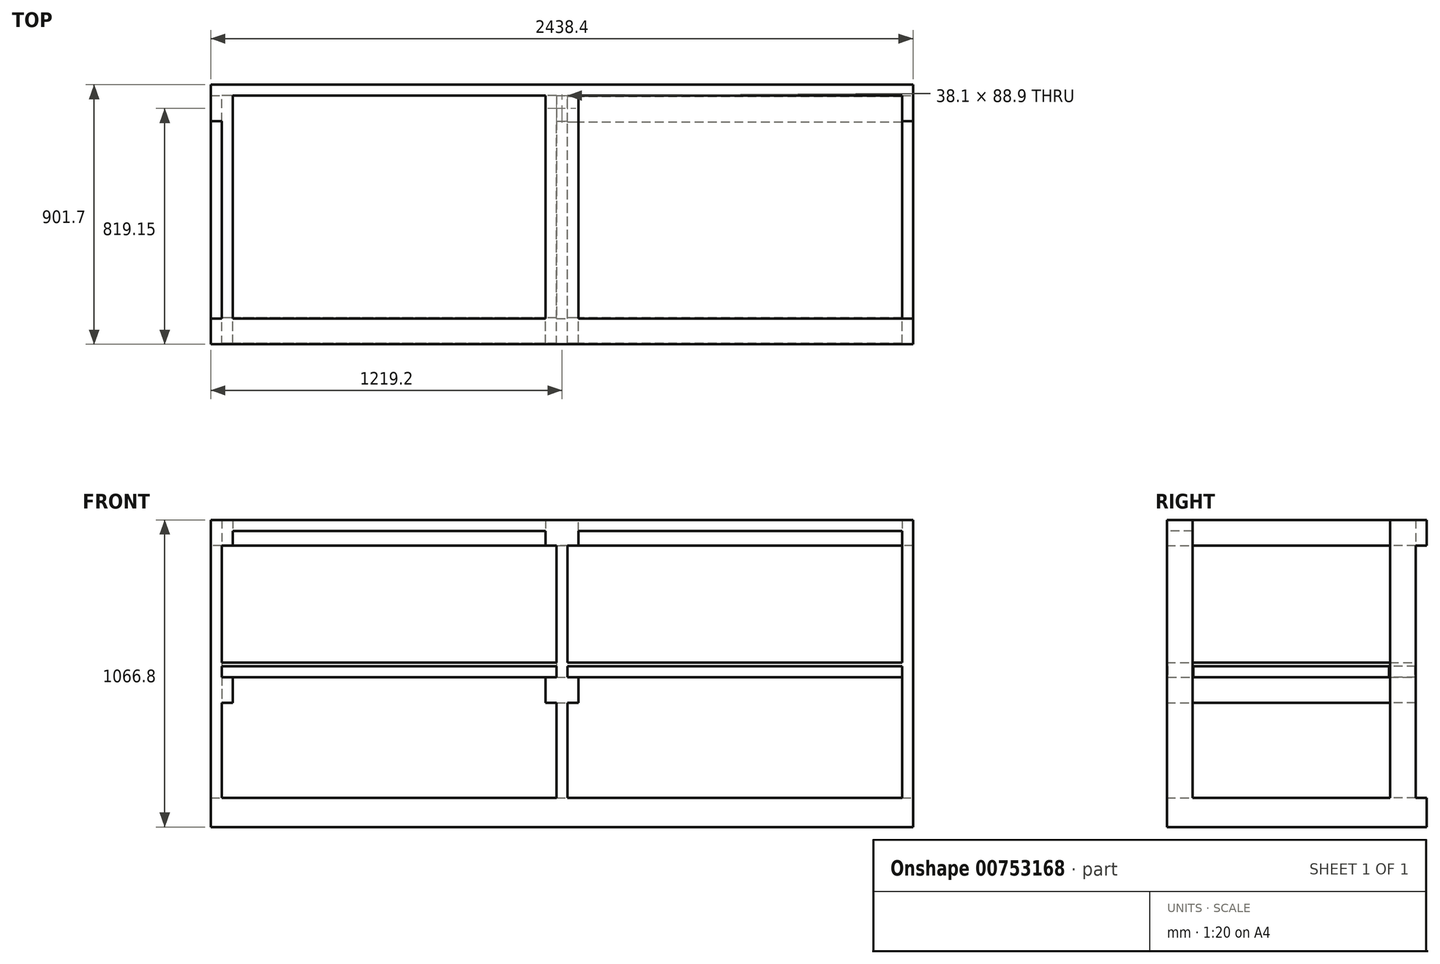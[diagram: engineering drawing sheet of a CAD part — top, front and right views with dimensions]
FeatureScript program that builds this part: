
annotation { "Feature Type Name" : "Feature", "Feature Type Description" : "" }
export const myFeature = defineFeature(function(context is Context, id is Id, definition is map)
    precondition{}
    {
        {
            var Q0;
            Q0=qCreatedBy(makeId("Top.planeOp"),FACE);
            var sketch = newSketch(context, id + "F0", { "sketchPlane" : qUnion([Q0])});
            skLineSegment(sketch, "E0.bottom", {"start": v(0, 0) * mm, "end": v(38.1, 0) * mm});
            skLineSegment(sketch, "E0.top", {"start": v(0, 88.9) * mm, "end": v(38.1, 88.9) * mm});
            skLineSegment(sketch, "E0.left", {"start": v(0, 0) * mm, "end": v(0, 88.9) * mm});
            skLineSegment(sketch, "E0.right", {"start": v(38.1, 0) * mm, "end": v(38.1, 88.9) * mm});
            skLineSegment(sketch, "E1.bottom", {"start": v(0, 774.7) * mm, "end": v(38.1, 774.7) * mm});
            skLineSegment(sketch, "E1.top", {"start": v(0, 863.6) * mm, "end": v(38.1, 863.6) * mm});
            skLineSegment(sketch, "E1.left", {"start": v(0, 774.7) * mm, "end": v(0, 863.6) * mm});
            skLineSegment(sketch, "E1.right", {"start": v(38.1, 774.7) * mm, "end": v(38.1, 863.6) * mm});
            skLineSegment(sketch, "E2.bottom", {"start": v(1200.15, 0) * mm, "end": v(1238.25, 0) * mm});
            skLineSegment(sketch, "E2.top", {"start": v(1200.15, 88.9) * mm, "end": v(1238.25, 88.9) * mm});
            skLineSegment(sketch, "E2.left", {"start": v(1200.15, 0) * mm, "end": v(1200.15, 88.9) * mm});
            skLineSegment(sketch, "E2.right", {"start": v(1238.25, 0) * mm, "end": v(1238.25, 88.9) * mm});
            skLineSegment(sketch, "E3.bottom", {"start": v(1200.15, 863.6) * mm, "end": v(1238.25, 863.6) * mm});
            skLineSegment(sketch, "E3.top", {"start": v(1200.15, 774.7) * mm, "end": v(1238.25, 774.7) * mm});
            skLineSegment(sketch, "E3.left", {"start": v(1200.15, 863.6) * mm, "end": v(1200.15, 774.7) * mm});
            skLineSegment(sketch, "E3.right", {"start": v(1238.25, 863.6) * mm, "end": v(1238.25, 774.7) * mm});
            skLineSegment(sketch, "E4.bottom", {"start": v(2400.3, 863.6) * mm, "end": v(2438.4, 863.6) * mm});
            skLineSegment(sketch, "E4.top", {"start": v(2400.3, 774.7) * mm, "end": v(2438.4, 774.7) * mm});
            skLineSegment(sketch, "E4.left", {"start": v(2400.3, 863.6) * mm, "end": v(2400.3, 774.7) * mm});
            skLineSegment(sketch, "E4.right", {"start": v(2438.4, 863.6) * mm, "end": v(2438.4, 774.7) * mm});
            skLineSegment(sketch, "E5.bottom", {"start": v(2400.3, 88.9) * mm, "end": v(2438.4, 88.9) * mm});
            skLineSegment(sketch, "E5.top", {"start": v(2400.3, 0) * mm, "end": v(2438.4, 0) * mm});
            skLineSegment(sketch, "E5.left", {"start": v(2400.3, 88.9) * mm, "end": v(2400.3, 0) * mm});
            skLineSegment(sketch, "E5.right", {"start": v(2438.4, 88.9) * mm, "end": v(2438.4, 0) * mm});
            skLineSegment(sketch, "E6", {"start": v(38.1, 0) * mm, "end": v(1200.15, 0) * mm});
            skLineSegment(sketch, "E7", {"start": v(1238.25, 0) * mm, "end": v(2400.3, 0) * mm});
            skLineSegment(sketch, "E8", {"start": v(0, 88.9) * mm, "end": v(0, 774.7) * mm});
            skLineSegment(sketch, "E9", {"start": v(38.1, 863.6) * mm, "end": v(1200.15, 863.6) * mm});
            skLineSegment(sketch, "E10", {"start": v(1238.25, 863.6) * mm, "end": v(2400.3, 863.6) * mm});
            skLineSegment(sketch, "E11", {"start": v(2438.4, 774.7) * mm, "end": v(2438.4, 88.9) * mm});
            skLineSegment(sketch, "E12", {"start": v(0, 863.6) * mm, "end": v(0, 901.7) * mm});
            skLineSegment(sketch, "E13", {"start": v(0, 901.7) * mm, "end": v(2438.4, 901.7) * mm});
            skLineSegment(sketch, "E14", {"start": v(2438.4, 901.7) * mm, "end": v(2438.4, 863.6) * mm});
            skSolve(sketch);
        }
        {
            var Q0;
            Q0=makeQuery(id+"F0.imprint","IMPRINT",FACE,{"disambiguationData":[TD([[makeQuery(id+"F0.imprint","IMPRINT",EDGE,{"derivedFrom":sQuery(id+"F0.wireOp",EDGE,"E0.top")}),1.0]])]});
            var Q1;
            Q1=makeQuery(id+"F0.imprint","IMPRINT",FACE,{"disambiguationData":[TD([[makeQuery(id+"F0.imprint","IMPRINT",EDGE,{"derivedFrom":sQuery(id+"F0.wireOp",EDGE,"E1.bottom")}),1.0]])]});
            var Q2;
            Q2=makeQuery(id+"F0.imprint","IMPRINT",FACE,{"disambiguationData":[TD([[makeQuery(id+"F0.imprint","IMPRINT",EDGE,{"derivedFrom":sQuery(id+"F0.wireOp",EDGE,"E3.bottom")}),-1.0]])]});
            var Q3;
            Q3=makeQuery(id+"F0.imprint","IMPRINT",FACE,{"disambiguationData":[TD([[makeQuery(id+"F0.imprint","IMPRINT",EDGE,{"derivedFrom":sQuery(id+"F0.wireOp",EDGE,"E4.bottom")}),-1.0]])]});
            var Q4;
            Q4=makeQuery(id+"F0.imprint","IMPRINT",FACE,{"disambiguationData":[TD([[makeQuery(id+"F0.imprint","IMPRINT",EDGE,{"derivedFrom":sQuery(id+"F0.wireOp",EDGE,"E5.bottom")}),-1.0]])]});
            var Q5;
            Q5=makeQuery(id+"F0.imprint","IMPRINT",FACE,{"disambiguationData":[TD([[makeQuery(id+"F0.imprint","IMPRINT",EDGE,{"derivedFrom":sQuery(id+"F0.wireOp",EDGE,"E2.bottom")}),1.0]])]});
            var Q6;
            Q6=makeQuery(id+"F0.imprint","IMPRINT",FACE,{"disambiguationData":[TD([[makeQuery(id+"F0.imprint","IMPRINT",EDGE,{"derivedFrom":sQuery(id+"F0.wireOp",EDGE,"E0.bottom")}),1.0]])]});
            var Q7;
            Q7=makeQuery(id+"F0.imprint","IMPRINT",FACE,{"disambiguationData":[TD([[makeQuery(id+"F0.imprint","IMPRINT",EDGE,{"derivedFrom":sQuery(id+"F0.wireOp",EDGE,"E1.top")}),1.0]])]});
            extrude(context, id + "F1", {"entities" : qUnion([Q0, Q1, Q2, Q3, Q4, Q5, Q6, Q7]), "oppositeDirection" : true, "depth" : 101.6 * mm, "offsetDistance" : 25.4 * mm});
        }
        {
            var Q0;
            Q0=makeQuery(id+"F0.imprint","IMPRINT",FACE,{"disambiguationData":[TD([[makeQuery(id+"F0.imprint","IMPRINT",EDGE,{"derivedFrom":sQuery(id+"F0.wireOp",EDGE,"E0.bottom")}),1.0]])]});
            var Q1;
            Q1=makeQuery(id+"F0.imprint","IMPRINT",FACE,{"disambiguationData":[TD([[makeQuery(id+"F0.imprint","IMPRINT",EDGE,{"derivedFrom":sQuery(id+"F0.wireOp",EDGE,"E5.bottom")}),-1.0]])]});
            var Q2;
            Q2=makeQuery(id+"F0.imprint","IMPRINT",FACE,{"disambiguationData":[TD([[makeQuery(id+"F0.imprint","IMPRINT",EDGE,{"derivedFrom":sQuery(id+"F0.wireOp",EDGE,"E2.bottom")}),1.0]])]});
            extrude(context, id + "F2", {"entities" : qUnion([Q0, Q1, Q2]), "operationType" : NewBodyOperationType.ADD, "depth" : 927.1 * mm, "offsetDistance" : 25.4 * mm});
        }
        {
            var Q0;
            Q0=makeQuery(id+"F2.opExtrude","CAP_FACE",FACE,{"disambiguationData":[OSD([sQuery(id+"F0.wireOp",EDGE,"E0.bottom"),sQuery(id+"F0.wireOp",EDGE,"E0.top"),sQuery(id+"F0.wireOp",EDGE,"E0.left"),sQuery(id+"F0.wireOp",EDGE,"E0.right")])],"isStart":false});
            var sketch = newSketch(context, id + "F3", { "sketchPlane" : qUnion([Q0])});
            skLineSegment(sketch, "E15.bottom", {"start": v(0, 0) * mm, "end": v(2438.4, 0) * mm});
            skLineSegment(sketch, "E15.top", {"start": v(0, 88.9) * mm, "end": v(2438.4, 88.9) * mm});
            skLineSegment(sketch, "E15.left", {"start": v(0, 0) * mm, "end": v(0, 88.9) * mm});
            skLineSegment(sketch, "E15.right", {"start": v(2438.4, 0) * mm, "end": v(2438.4, 88.9) * mm});
            skSolve(sketch);
        }
        {
            var Q0;
            Q0 = qSketchRegion(id + "F3", true);
            extrude(context, id + "F4", {"entities" : qUnion([Q0]), "operationType" : NewBodyOperationType.ADD, "depth" : 38.1 * mm, "offsetDistance" : 25.4 * mm});
        }
        {
            var Q0;
            Q0=makeQuery(id+"F0.imprint","IMPRINT",FACE,{"disambiguationData":[TD([[makeQuery(id+"F0.imprint","IMPRINT",EDGE,{"derivedFrom":sQuery(id+"F0.wireOp",EDGE,"E1.bottom")}),1.0]])]});
            var Q1;
            Q1=makeQuery(id+"F0.imprint","IMPRINT",FACE,{"disambiguationData":[TD([[makeQuery(id+"F0.imprint","IMPRINT",EDGE,{"derivedFrom":sQuery(id+"F0.wireOp",EDGE,"E3.bottom")}),-1.0]])]});
            var Q2;
            Q2=makeQuery(id+"F0.imprint","IMPRINT",FACE,{"disambiguationData":[TD([[makeQuery(id+"F0.imprint","IMPRINT",EDGE,{"derivedFrom":sQuery(id+"F0.wireOp",EDGE,"E4.bottom")}),-1.0]])]});
            extrude(context, id + "F5", {"entities" : qUnion([Q0, Q1, Q2]), "operationType" : NewBodyOperationType.ADD, "depth" : 965.2 * mm, "offsetDistance" : 25.4 * mm});
        }
        {
            var Q0;
            Q0=makeQuery(id+"F5.opExtrude","SWEPT_FACE",FACE,{"disambiguationData":[OSD([sQuery(id+"F0.wireOp",EDGE,"E4.bottom")])]});
            var sketch = newSketch(context, id + "F6", { "sketchPlane" : qUnion([Q0])});
            skLineSegment(sketch, "E16.bottom", {"start": v(-2438.4, 965.2) * mm, "end": v(0, 965.2) * mm});
            skLineSegment(sketch, "E16.top", {"start": v(-2438.4, 876.3) * mm, "end": v(0, 876.3) * mm});
            skLineSegment(sketch, "E16.left", {"start": v(-2438.4, 965.2) * mm, "end": v(-2438.4, 876.3) * mm});
            skLineSegment(sketch, "E16.right", {"start": v(0, 965.2) * mm, "end": v(0, 876.3) * mm});
            skSolve(sketch);
        }
        {
            var Q0;
            Q0 = qSketchRegion(id + "F6", true);
            extrude(context, id + "F7", {"entities" : qUnion([Q0]), "operationType" : NewBodyOperationType.ADD, "depth" : 38.1 * mm, "offsetDistance" : 25.4 * mm});
        }
        {
            var Q0;
            Q0=makeQuery(id+"F2.opExtrude","SWEPT_FACE",FACE,{"disambiguationData":[OSD([sQuery(id+"F0.wireOp",EDGE,"E0.right")])]});
            var sketch = newSketch(context, id + "F8", { "sketchPlane" : qUnion([Q0])});
            skLineSegment(sketch, "E17.bottom", {"start": v(0, 965.2) * mm, "end": v(863.6, 965.2) * mm});
            skLineSegment(sketch, "E17.top", {"start": v(0, 876.3) * mm, "end": v(863.6, 876.3) * mm});
            skLineSegment(sketch, "E17.left", {"start": v(0, 965.2) * mm, "end": v(0, 876.3) * mm});
            skLineSegment(sketch, "E17.right", {"start": v(863.6, 965.2) * mm, "end": v(863.6, 876.3) * mm});
            skLineSegment(sketch, "E18.bottom", {"start": v(0, 419.1) * mm, "end": v(863.6, 419.1) * mm});
            skLineSegment(sketch, "E18.top", {"start": v(0, 330.2) * mm, "end": v(863.6, 330.2) * mm});
            skLineSegment(sketch, "E18.left", {"start": v(0, 419.1) * mm, "end": v(0, 330.2) * mm});
            skLineSegment(sketch, "E18.right", {"start": v(863.6, 419.1) * mm, "end": v(863.6, 330.2) * mm});
            skLineSegment(sketch, "E19.bottom", {"start": v(863.6, 419.1) * mm, "end": v(774.7, 419.1) * mm});
            skLineSegment(sketch, "E19.top", {"start": v(863.6, 457.2) * mm, "end": v(774.7, 457.2) * mm});
            skLineSegment(sketch, "E19.left", {"start": v(863.6, 419.1) * mm, "end": v(863.6, 457.2) * mm});
            skLineSegment(sketch, "E19.right", {"start": v(774.7, 419.1) * mm, "end": v(774.7, 457.2) * mm});
            skLineSegment(sketch, "E20.bottom", {"start": v(0, 457.2) * mm, "end": v(863.6, 457.2) * mm});
            skLineSegment(sketch, "E20.top", {"start": v(0, 469.9) * mm, "end": v(863.6, 469.9) * mm});
            skLineSegment(sketch, "E20.left", {"start": v(0, 457.2) * mm, "end": v(0, 469.9) * mm});
            skLineSegment(sketch, "E20.right", {"start": v(863.6, 457.2) * mm, "end": v(863.6, 469.9) * mm});
            skLineSegment(sketch, "E21", {"start": v(3.17, 419.1) * mm, "end": v(3.17, 457.2) * mm});
            skLineSegment(sketch, "E22", {"start": v(92.08, 457.2) * mm, "end": v(92.08, 419.1) * mm});
            skSolve(sketch);
        }
        {
            var Q0;
            {var subQ0=sQuery(id+"F8.wireOp",EDGE,"E17.left");Q0=makeQuery(id+"F8.imprint","IMPRINT",FACE,{"disambiguationData":[TD([[makeQuery(id+"F8.imprint","IMPRINT",EDGE,{"derivedFrom":subQ0}),1.0]])]});}
            var Q1;
            {var subQ3=sQuery(id+"F8.wireOp",EDGE,"E17.right");Q1=makeQuery(id+"F8.imprint","IMPRINT",FACE,{"disambiguationData":[TD([[makeQuery(id+"F8.imprint","IMPRINT",EDGE,{"derivedFrom":subQ3}),-1.0]])]});}
            var Q2;
            {var subQ0=sQuery(id+"F8.wireOp",EDGE,"E18.left");Q2=makeQuery(id+"F8.imprint","IMPRINT",FACE,{"disambiguationData":[TD([[makeQuery(id+"F8.imprint","IMPRINT",EDGE,{"derivedFrom":subQ0}),1.0]])]});}
            var Q3;
            {var subQ0=sQuery(id+"F8.wireOp",EDGE,"E18.right");Q3=makeQuery(id+"F8.imprint","IMPRINT",FACE,{"disambiguationData":[TD([[makeQuery(id+"F8.imprint","IMPRINT",EDGE,{"derivedFrom":subQ0}),-1.0]])]});}
            extrude(context, id + "F9", {"entities" : qUnion([Q0, Q1, Q2, Q3]), "operationType" : NewBodyOperationType.ADD, "depth" : 38.1 * mm, "offsetDistance" : 25.4 * mm});
        }
        {
            var Q0;
            {var subQ0=sQuery(id+"F8.wireOp",EDGE,"E20.left");Q0=makeQuery(id+"F8.imprint","IMPRINT",FACE,{"disambiguationData":[TD([[makeQuery(id+"F8.imprint","IMPRINT",EDGE,{"derivedFrom":subQ0}),1.0]])]});}
            var Q1;
            {var subQ0=sQuery(id+"F8.wireOp",EDGE,"E20.right");Q1=makeQuery(id+"F8.imprint","IMPRINT",FACE,{"disambiguationData":[TD([[makeQuery(id+"F8.imprint","IMPRINT",EDGE,{"derivedFrom":subQ0}),1.0]])]});}
            var Q2;
            Q2=makeQuery(id+"F8.imprint","IMPRINT",FACE,{"disambiguationData":[TD([[makeQuery(id+"F8.imprint","IMPRINT",EDGE,{"derivedFrom":sQuery(id+"F8.wireOp",EDGE,"E19.bottom")}),-1.0]])]});
            var Q3;
            {var subQ0=sQuery(id+"F8.wireOp",EDGE,"E22");Q3=makeQuery(id+"F8.imprint","IMPRINT",FACE,{"disambiguationData":[TD([[makeQuery(id+"F8.imprint","IMPRINT",EDGE,{"derivedFrom":subQ0}),-1.0]])]});}
            var Q4;
            {var subQ0=sQuery(id+"F8.wireOp",EDGE,"E21");Q4=makeQuery(id+"F8.imprint","IMPRINT",FACE,{"disambiguationData":[TD([[makeQuery(id+"F8.imprint","IMPRINT",EDGE,{"derivedFrom":subQ0}),-1.0]])]});}
            var Q5;
            Q5=makeQuery(id+"F5.opExtrude","SWEPT_FACE",FACE,{"disambiguationData":[OSD([sQuery(id+"F0.wireOp",EDGE,"E3.left")])]});
            extrude(context, id + "F10", {"entities" : qUnion([Q0, Q1, Q2, Q3, Q4]), "operationType" : NewBodyOperationType.ADD, "endBound" : BoundingType.UP_TO_SURFACE, "depth" : 25.4 * mm, "endBoundEntityFace" : qUnion([Q5]), "offsetDistance" : 25.4 * mm});
        }
        {
            var Q0;
            Q0=makeQuery(id+"F2.opExtrude","SWEPT_FACE",FACE,{"disambiguationData":[OSD([sQuery(id+"F0.wireOp",EDGE,"E2.right")])]});
            var sketch = newSketch(context, id + "F11", { "sketchPlane" : qUnion([Q0])});
            skLineSegment(sketch, "E23.bottom", {"start": v(0, 876.3) * mm, "end": v(863.6, 876.3) * mm});
            skLineSegment(sketch, "E23.top", {"start": v(0, 965.2) * mm, "end": v(863.6, 965.2) * mm});
            skLineSegment(sketch, "E23.left", {"start": v(0, 876.3) * mm, "end": v(0, 965.2) * mm});
            skLineSegment(sketch, "E23.right", {"start": v(863.6, 876.3) * mm, "end": v(863.6, 965.2) * mm});
            skLineSegment(sketch, "E24.bottom", {"start": v(0, 330.2) * mm, "end": v(863.6, 330.2) * mm});
            skLineSegment(sketch, "E24.top", {"start": v(0, 419.1) * mm, "end": v(863.6, 419.1) * mm});
            skLineSegment(sketch, "E24.left", {"start": v(0, 330.2) * mm, "end": v(0, 419.1) * mm});
            skLineSegment(sketch, "E24.right", {"start": v(863.6, 330.2) * mm, "end": v(863.6, 419.1) * mm});
            skSolve(sketch);
        }
        {
            var Q0;
            Q0 = qSketchRegion(id + "F11", true);
            extrude(context, id + "F12", {"entities" : qUnion([Q0]), "operationType" : NewBodyOperationType.ADD, "depth" : 38.1 * mm, "offsetDistance" : 25.4 * mm, "hasSecondDirection" : true, "secondDirectionOppositeDirection" : true, "secondDirectionDepth" : 76.2 * mm});
        }
        {
            var Q0;
            Q0=makeQuery(id+"F12.boolean.opBoolean","SPLIT",FACE,{"disambiguationData":[TD([makeQuery(id+"F7.opExtrude","SWEPT_FACE",FACE,{"disambiguationData":[OSD([sQuery(id+"F6.wireOp",EDGE,"E16.top")])]})])],"derivedFrom":makeQuery(id+"F2.opExtrude","SWEPT_FACE",FACE,{"disambiguationData":[OSD([sQuery(id+"F0.wireOp",EDGE,"E2.right")])]})});
            var sketch = newSketch(context, id + "F13", { "sketchPlane" : qUnion([Q0])});
            skLineSegment(sketch, "E25.bottom", {"start": v(0, 469.9) * mm, "end": v(863.6, 469.9) * mm});
            skLineSegment(sketch, "E25.top", {"start": v(0, 457.2) * mm, "end": v(863.6, 457.2) * mm});
            skLineSegment(sketch, "E25.left", {"start": v(0, 469.9) * mm, "end": v(0, 457.2) * mm});
            skLineSegment(sketch, "E25.right", {"start": v(863.6, 469.9) * mm, "end": v(863.6, 457.2) * mm});
            skLineSegment(sketch, "E26.bottom", {"start": v(3.17, 457.2) * mm, "end": v(92.07, 457.2) * mm});
            skLineSegment(sketch, "E26.top", {"start": v(3.17, 419.1) * mm, "end": v(92.07, 419.1) * mm});
            skLineSegment(sketch, "E26.left", {"start": v(3.17, 457.2) * mm, "end": v(3.17, 419.1) * mm});
            skLineSegment(sketch, "E26.right", {"start": v(92.07, 457.2) * mm, "end": v(92.07, 419.1) * mm});
            skLineSegment(sketch, "E27.bottom", {"start": v(771.52, 457.2) * mm, "end": v(860.42, 457.2) * mm});
            skLineSegment(sketch, "E27.top", {"start": v(771.52, 419.1) * mm, "end": v(860.42, 419.1) * mm});
            skLineSegment(sketch, "E27.left", {"start": v(771.52, 457.2) * mm, "end": v(771.52, 419.1) * mm});
            skLineSegment(sketch, "E27.right", {"start": v(860.42, 457.2) * mm, "end": v(860.42, 419.1) * mm});
            skSolve(sketch);
        }
        {
            var Q0;
            Q0 = qSketchRegion(id + "F13", true);
            var Q1;
            Q1=makeQuery(id+"F5.opExtrude","SWEPT_FACE",FACE,{"disambiguationData":[OSD([sQuery(id+"F0.wireOp",EDGE,"E4.left")])]});
            extrude(context, id + "F14", {"entities" : qUnion([Q0]), "operationType" : NewBodyOperationType.ADD, "endBound" : BoundingType.UP_TO_SURFACE, "depth" : 25.4 * mm, "endBoundEntityFace" : qUnion([Q1]), "offsetDistance" : 25.4 * mm});
        }
    });
